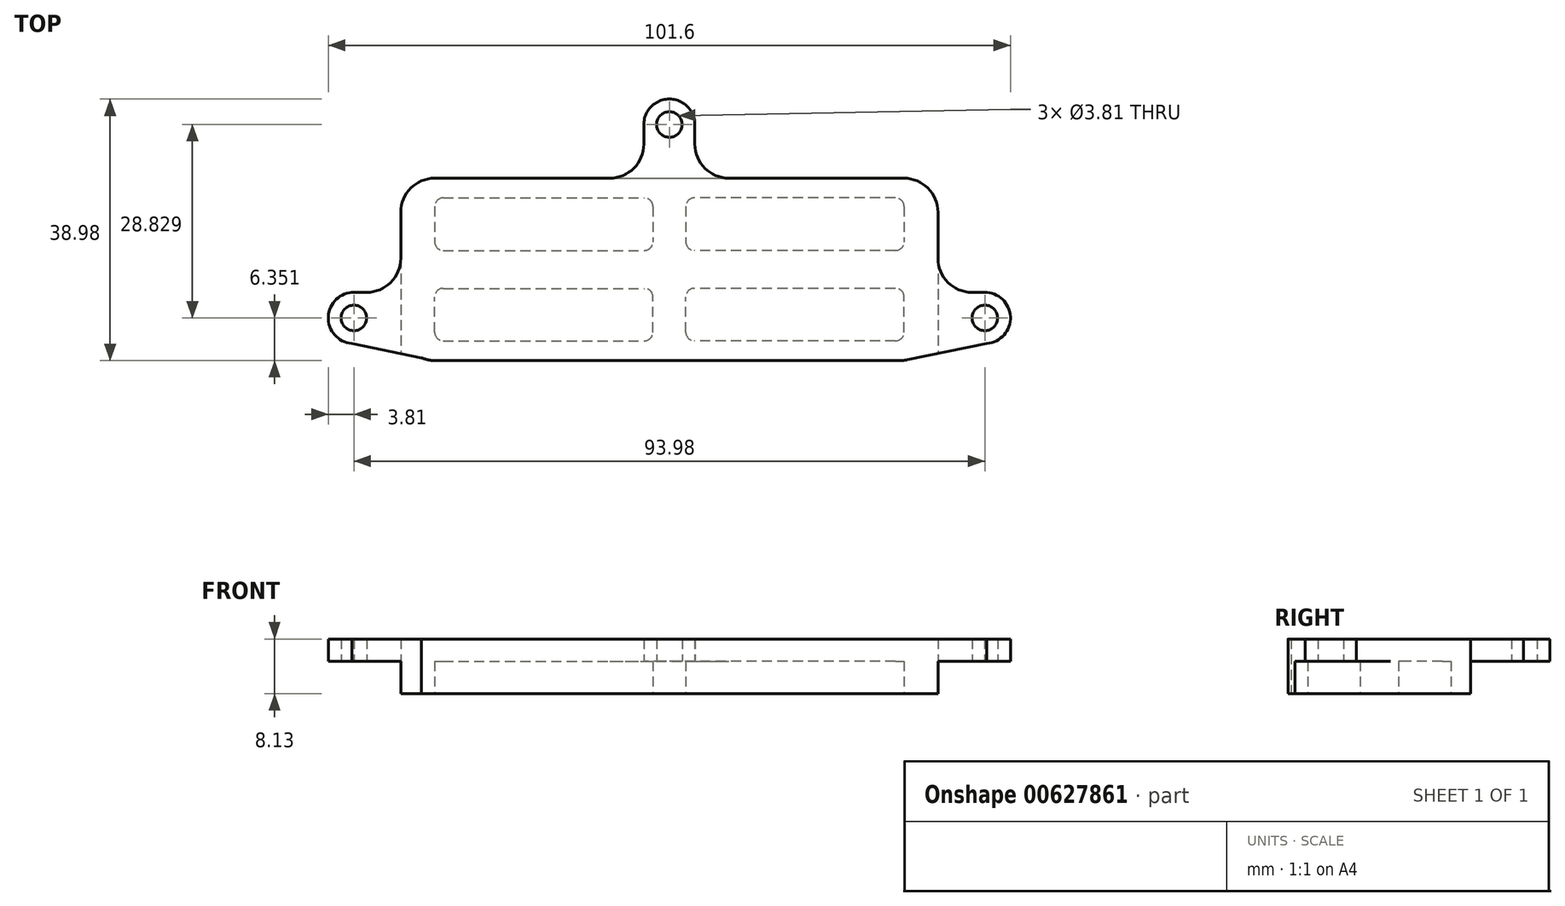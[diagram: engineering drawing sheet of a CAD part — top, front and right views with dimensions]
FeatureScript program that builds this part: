
annotation { "Feature Type Name" : "Feature", "Feature Type Description" : "" }
export const myFeature = defineFeature(function(context is Context, id is Id, definition is map)
    precondition{}
    {
        {
            var Q0;
            Q0=qCreatedBy(makeId("Top.planeOp"),FACE);
            var sketch = newSketch(context, id + "F0", { "sketchPlane" : qUnion([Q0])});
            skLineSegment(sketch, "E0.bottom", {"start": v(-34.93, 13.59) * mm, "end": v(-8.88, 13.59) * mm});
            skLineSegment(sketch, "E0.top", {"start": v(-34.93, -13.59) * mm, "end": v(34.4, -13.59) * mm});
            skLineSegment(sketch, "E0.left", {"start": v(-40, 8.5) * mm, "end": v(-40, 1.65) * mm});
            skLineSegment(sketch, "E0.right", {"start": v(40, 8.5) * mm, "end": v(40, 1.65) * mm});
            skPoint(sketch, "E0.middle", {"position": v(0, 0) * mm});
            skPoint(sketch, "E1", {"position": v(-47, -7.24) * mm});
            skPoint(sketch, "E2.MirrorP", {"position": v(47, -7.24) * mm});
            skPoint(sketch, "E3", {"position": v(0, 21.59) * mm});
            skPoint(sketch, "E4", {"position": v(-9.31, -13.59) * mm});
            skPoint(sketch, "E5.visualSharp", {"position": v(-40, 13.59) * mm});
            skArc(sketch, "E5.filletArc", {"start": v(-34.93, 13.59) * mm, "mid": v(-38.52, 12.1) * mm, "end": v(-40, 8.5) * mm});
            skArc(sketch, "E6.MirrorCS", {"start": v(-34.93, -13.59) * mm, "mid": v(-35.95, -13.48) * mm, "end": v(-36.94, -13.17) * mm});
            skArc(sketch, "E7.MirrorCS", {"start": v(34.93, 13.59) * mm, "mid": v(38.52, 12.1) * mm, "end": v(40, 8.5) * mm});
            skCircle(sketch, "E8", {"center": v(47, -7.24) * mm, "radius": 3.81 * mm});
            skCircle(sketch, "E9", {"center": v(-47, -7.24) * mm, "radius": 3.81 * mm});
            skCircle(sketch, "E10", {"center": v(0, 21.59) * mm, "radius": 3.8 * mm});
            skPoint(sketch, "E11.orphan", {"position": v(40, 13.59) * mm});
            skPoint(sketch, "E12.orphan", {"position": v(40, -13.59) * mm});
            skLineSegment(sketch, "E13", {"start": v(-3.8, 21.72) * mm, "end": v(-3.8, 18.67) * mm});
            skArc(sketch, "E14.filletArc", {"start": v(-8.88, 13.59) * mm, "mid": v(-5.29, 15.08) * mm, "end": v(-3.8, 18.67) * mm});
            skArc(sketch, "E15.MirrorCS", {"start": v(8.88, 13.59) * mm, "mid": v(5.29, 15.08) * mm, "end": v(3.8, 18.67) * mm});
            skLineSegment(sketch, "E16.MirrorCS", {"start": v(3.8, 21.72) * mm, "end": v(3.8, 18.67) * mm});
            skLineSegment(sketch, "E17", {"start": v(-47.04, -3.43) * mm, "end": v(-45.09, -3.43) * mm});
            skPoint(sketch, "E17.endSnap0", {"position": v(-40, -2.54) * mm});
            skPoint(sketch, "E18.newPointA", {"position": v(-40, -3.43) * mm});
            skPoint(sketch, "E18.newPointB", {"position": v(-40, -13.59) * mm});
            skArc(sketch, "E18.filletArc", {"start": v(-45.09, -3.43) * mm, "mid": v(-41.5, -1.94) * mm, "end": v(-40, 1.65) * mm});
            skArc(sketch, "E19.MirrorCS", {"start": v(45.09, -3.43) * mm, "mid": v(41.5, -1.94) * mm, "end": v(40, 1.65) * mm});
            skLineSegment(sketch, "E20.MirrorCS", {"start": v(47.04, -3.43) * mm, "end": v(45.09, -3.43) * mm});
            skLineSegment(sketch, "E21", {"start": v(47.3, -11.04) * mm, "end": v(35.43, -13.48) * mm});
            skPoint(sketch, "E22.orphan", {"position": v(40, -8.5) * mm});
            skPoint(sketch, "E23.visualSharp", {"position": v(34.93, -13.59) * mm});
            skArc(sketch, "E23.filletArc", {"start": v(34.4, -13.59) * mm, "mid": v(34.92, -13.56) * mm, "end": v(35.43, -13.48) * mm});
            skLineSegment(sketch, "E24.MirrorCS", {"start": v(-47.3, -11.04) * mm, "end": v(-35.43, -13.48) * mm});
            skPoint(sketch, "E25.orphan", {"position": v(-40, -8.5) * mm});
            skCircle(sketch, "E26", {"center": v(0, 21.59) * mm, "radius": 1.9 * mm});
            skCircle(sketch, "E27", {"center": v(-47, -7.24) * mm, "radius": 1.9 * mm});
            skCircle(sketch, "E28", {"center": v(47, -7.24) * mm, "radius": 1.9 * mm});
            skPoint(sketch, "E29.visualSharp", {"position": v(-34.16, 7.75) * mm});
            skPoint(sketch, "E30.orphan", {"position": v(-34.16, -7.75) * mm});
            skPoint(sketch, "E31.orphan", {"position": v(34.16, -7.75) * mm});
            skPoint(sketch, "E32.orphan", {"position": v(34.16, 7.75) * mm});
            skLineSegment(sketch, "E33", {"start": v(8.88, 13.59) * mm, "end": v(34.93, 13.59) * mm});
            skPoint(sketch, "E29.filletArc.end.orphan", {"position": v(-34.16, 5.2) * mm});
            skPoint(sketch, "E29.filletArc.start.orphan", {"position": v(-31.62, 7.75) * mm});
            skPoint(sketch, "E34.MirrorCS.end.orphan", {"position": v(-34.16, -5.2) * mm});
            skPoint(sketch, "E35.top.start.orphan", {"position": v(-31.62, -7.75) * mm});
            skPoint(sketch, "E36.MirrorCS.start.orphan", {"position": v(31.62, -7.75) * mm});
            skPoint(sketch, "E35.right.end.orphan", {"position": v(34.16, -5.2) * mm});
            skPoint(sketch, "E37.MirrorCS.end.orphan", {"position": v(34.16, 5.2) * mm});
            skPoint(sketch, "E37.MirrorCS.start.orphan", {"position": v(31.62, 7.75) * mm});
            skLineSegment(sketch, "E38", {"start": v(-40, 1.65) * mm, "end": v(-40, -12.54) * mm});
            skSolve(sketch);
        }
        {
            var Q0;
            Q0=qSketchRegion(id+"F0",true);
            extrude(context, id + "F1", {"entities" : qUnion([Q0]), "depth" : 3.3 * mm, "offsetDistance" : 25.4 * mm});
        }
        {
            var Q0;
            Q0=makeQuery(id+"F1.opExtrude","CAP_FACE",FACE,{"disambiguationData":[OSD([sQuery(id+"F0.wireOp",EDGE,"E0.bottom"),sQuery(id+"F0.wireOp",EDGE,"E0.top"),sQuery(id+"F0.wireOp",EDGE,"E0.left"),sQuery(id+"F0.wireOp",EDGE,"E0.right"),sQuery(id+"F0.wireOp",EDGE,"E5.filletArc"),sQuery(id+"F0.wireOp",EDGE,"E6.MirrorCS"),sQuery(id+"F0.wireOp",EDGE,"E7.MirrorCS"),sQuery(id+"F0.wireOp",EDGE,"E8"),sQuery(id+"F0.wireOp",EDGE,"E9"),sQuery(id+"F0.wireOp",EDGE,"E10"),sQuery(id+"F0.wireOp",EDGE,"E13"),sQuery(id+"F0.wireOp",EDGE,"E14.filletArc"),sQuery(id+"F0.wireOp",EDGE,"E15.MirrorCS"),sQuery(id+"F0.wireOp",EDGE,"E16.MirrorCS"),sQuery(id+"F0.wireOp",EDGE,"E17"),sQuery(id+"F0.wireOp",EDGE,"E18.filletArc"),sQuery(id+"F0.wireOp",EDGE,"E19.MirrorCS"),sQuery(id+"F0.wireOp",EDGE,"E20.MirrorCS"),sQuery(id+"F0.wireOp",EDGE,"E21"),sQuery(id+"F0.wireOp",EDGE,"E23.filletArc"),sQuery(id+"F0.wireOp",EDGE,"E24.MirrorCS"),sQuery(id+"F0.wireOp",EDGE,"E26"),sQuery(id+"F0.wireOp",EDGE,"E27"),sQuery(id+"F0.wireOp",EDGE,"E28"),sQuery(id+"F0.wireOp",EDGE,"E33")])],"isStart":true});
            var sketch = newSketch(context, id + "F2", { "sketchPlane" : qUnion([Q0])});
            skLineSegment(sketch, "E39", {"start": v(-40, -5.08) * mm, "end": v(-40, 12.54) * mm});
            skLineSegment(sketch, "E40.MirrorCS", {"start": v(40, -5.08) * mm, "end": v(40, 12.54) * mm});
            skLineSegment(sketch, "E41", {"start": v(-13.13, -13.59) * mm, "end": v(9.64, -13.59) * mm});
            skSolve(sketch);
        }
        {
            var Q0;
            Q0=qSketchRegion(id+"F2",true);
            var Q1;
            Q1=makeQuery(id+"F2.imprint","IMPRINT",FACE,{"disambiguationData":[TD([[makeQuery(id+"F2.imprint","IMPRINT",EDGE,{"derivedFrom":makeQuery(id+"F1.opExtrude","CAP_EDGE",EDGE,{"disambiguationData":[OSD([sQuery(id+"F0.wireOp",EDGE,"E0.top")])],"isStart":true})}),-1.0]])]});
            extrude(context, id + "F3", {"entities" : qUnion([Q0, Q1]), "operationType" : NewBodyOperationType.ADD, "depth" : 4.83 * mm, "offsetDistance" : 25.4 * mm});
        }
        {
            var Q0;
            Q0=makeQuery(id+"F3.opExtrude","CAP_FACE",FACE,{"disambiguationData":[OSD([sQuery(id+"F0.wireOp",EDGE,"E0.bottom"),sQuery(id+"F0.wireOp",EDGE,"E0.top"),sQuery(id+"F0.wireOp",EDGE,"E0.right"),sQuery(id+"F0.wireOp",EDGE,"E5.filletArc"),sQuery(id+"F0.wireOp",EDGE,"E6.MirrorCS"),sQuery(id+"F0.wireOp",EDGE,"E7.MirrorCS"),sQuery(id+"F0.wireOp",EDGE,"E21"),sQuery(id+"F0.wireOp",EDGE,"E23.filletArc"),sQuery(id+"F0.wireOp",EDGE,"E24.MirrorCS"),sQuery(id+"F2.wireOp",EDGE,"E39"),sQuery(id+"F2.wireOp",EDGE,"E40.MirrorCS"),sQuery(id+"F2.wireOp",EDGE,"E41")])],"isStart":false});
            var sketch = newSketch(context, id + "F4", { "sketchPlane" : qUnion([Q0])});
            skLineSegment(sketch, "E42.MirrorCS", {"start": v(-33.69, -2.83) * mm, "end": v(-3.72, -2.83) * mm});
            skLineSegment(sketch, "E43.MirrorCS", {"start": v(-2.45, -9.38) * mm, "end": v(-2.45, -4.1) * mm});
            skLineSegment(sketch, "E44.MirrorCS", {"start": v(-33.69, -10.65) * mm, "end": v(-3.72, -10.65) * mm});
            skLineSegment(sketch, "E45.MirrorCS", {"start": v(-34.96, -9.38) * mm, "end": v(-34.96, -4.1) * mm});
            skPoint(sketch, "E46.visualSharp", {"position": v(-34.96, -2.83) * mm});
            skArc(sketch, "E46.filletArc", {"start": v(-33.69, -2.83) * mm, "mid": v(-34.58, -3.2) * mm, "end": v(-34.96, -4.1) * mm});
            skPoint(sketch, "E47.visualSharp", {"position": v(-2.45, -2.83) * mm});
            skArc(sketch, "E47.filletArc", {"start": v(-2.45, -4.1) * mm, "mid": v(-2.82, -3.2) * mm, "end": v(-3.72, -2.83) * mm});
            skPoint(sketch, "E48.visualSharp", {"position": v(-2.45, -10.65) * mm});
            skArc(sketch, "E48.filletArc", {"start": v(-3.72, -10.65) * mm, "mid": v(-2.82, -10.27) * mm, "end": v(-2.45, -9.38) * mm});
            skPoint(sketch, "E49.visualSharp", {"position": v(-34.96, -10.65) * mm});
            skArc(sketch, "E49.filletArc", {"start": v(-34.96, -9.38) * mm, "mid": v(-34.58, -10.27) * mm, "end": v(-33.69, -10.65) * mm});
            skLineSegment(sketch, "E50.MirrorCS", {"start": v(2.45, -9.38) * mm, "end": v(2.45, -4.1) * mm});
            skArc(sketch, "E51.MirrorCS", {"start": v(2.45, -4.1) * mm, "mid": v(2.82, -3.2) * mm, "end": v(3.72, -2.83) * mm});
            skArc(sketch, "E52.MirrorCS", {"start": v(3.72, -10.65) * mm, "mid": v(2.82, -10.27) * mm, "end": v(2.45, -9.38) * mm});
            skLineSegment(sketch, "E53.MirrorCS", {"start": v(33.69, -10.65) * mm, "end": v(3.72, -10.65) * mm});
            skArc(sketch, "E54.MirrorCS", {"start": v(34.96, -9.38) * mm, "mid": v(34.58, -10.27) * mm, "end": v(33.69, -10.65) * mm});
            skLineSegment(sketch, "E55.MirrorCS", {"start": v(34.96, -9.38) * mm, "end": v(34.96, -4.1) * mm});
            skArc(sketch, "E56.MirrorCS", {"start": v(33.69, -2.83) * mm, "mid": v(34.58, -3.2) * mm, "end": v(34.96, -4.1) * mm});
            skLineSegment(sketch, "E57.MirrorCS", {"start": v(33.69, -2.83) * mm, "end": v(3.72, -2.83) * mm});
            skLineSegment(sketch, "E58.MirrorCS", {"start": v(-33.69, 2.83) * mm, "end": v(-3.72, 2.83) * mm});
            skArc(sketch, "E59.MirrorCS", {"start": v(-2.45, 4.1) * mm, "mid": v(-2.82, 3.2) * mm, "end": v(-3.72, 2.83) * mm});
            skLineSegment(sketch, "E60.MirrorCS", {"start": v(-2.45, 9.38) * mm, "end": v(-2.45, 4.1) * mm});
            skArc(sketch, "E61.MirrorCS", {"start": v(-3.72, 10.65) * mm, "mid": v(-2.82, 10.27) * mm, "end": v(-2.45, 9.38) * mm});
            skLineSegment(sketch, "E62.MirrorCS", {"start": v(-33.69, 10.65) * mm, "end": v(-3.72, 10.65) * mm});
            skArc(sketch, "E63.MirrorCS", {"start": v(-34.96, 9.38) * mm, "mid": v(-34.58, 10.27) * mm, "end": v(-33.69, 10.65) * mm});
            skLineSegment(sketch, "E64.MirrorCS", {"start": v(-34.96, 9.38) * mm, "end": v(-34.96, 4.1) * mm});
            skArc(sketch, "E65.MirrorCS", {"start": v(-33.69, 2.83) * mm, "mid": v(-34.58, 3.2) * mm, "end": v(-34.96, 4.1) * mm});
            skLineSegment(sketch, "E66.MirrorCS", {"start": v(2.45, 9.38) * mm, "end": v(2.45, 4.1) * mm});
            skArc(sketch, "E67.MirrorCS", {"start": v(3.72, 10.65) * mm, "mid": v(2.82, 10.27) * mm, "end": v(2.45, 9.38) * mm});
            skLineSegment(sketch, "E68.MirrorCS", {"start": v(33.69, 10.65) * mm, "end": v(3.72, 10.65) * mm});
            skArc(sketch, "E69.MirrorCS", {"start": v(34.96, 9.38) * mm, "mid": v(34.58, 10.27) * mm, "end": v(33.69, 10.65) * mm});
            skLineSegment(sketch, "E70.MirrorCS", {"start": v(34.96, 9.38) * mm, "end": v(34.96, 4.1) * mm});
            skArc(sketch, "E71.MirrorCS", {"start": v(33.69, 2.83) * mm, "mid": v(34.58, 3.2) * mm, "end": v(34.96, 4.1) * mm});
            skLineSegment(sketch, "E72.MirrorCS", {"start": v(33.69, 2.83) * mm, "end": v(3.72, 2.83) * mm});
            skArc(sketch, "E73.MirrorCS", {"start": v(2.45, 4.1) * mm, "mid": v(2.82, 3.2) * mm, "end": v(3.72, 2.83) * mm});
            skSolve(sketch);
        }
        {
            var Q0;
            Q0=makeQuery(id+"F4.imprint","IMPRINT",FACE,{"disambiguationData":[TD([[makeQuery(id+"F4.imprint","IMPRINT",EDGE,{"derivedFrom":sQuery(id+"F4.wireOp",EDGE,"E58.MirrorCS")}),1.0]])]});
            var Q1;
            Q1=makeQuery(id+"F4.imprint","IMPRINT",FACE,{"disambiguationData":[TD([[makeQuery(id+"F4.imprint","IMPRINT",EDGE,{"derivedFrom":sQuery(id+"F4.wireOp",EDGE,"E66.MirrorCS")}),1.0]])]});
            var Q2;
            Q2=makeQuery(id+"F4.imprint","IMPRINT",FACE,{"disambiguationData":[TD([[makeQuery(id+"F4.imprint","IMPRINT",EDGE,{"derivedFrom":sQuery(id+"F4.wireOp",EDGE,"E42.MirrorCS")}),-1.0]])]});
            var Q3;
            Q3=makeQuery(id+"F4.imprint","IMPRINT",FACE,{"disambiguationData":[TD([[makeQuery(id+"F4.imprint","IMPRINT",EDGE,{"derivedFrom":sQuery(id+"F4.wireOp",EDGE,"E50.MirrorCS")}),-1.0]])]});
            extrude(context, id + "F5", {"entities" : qUnion([Q0, Q1, Q2, Q3]), "operationType" : NewBodyOperationType.REMOVE, "oppositeDirection" : true, "depth" : 4.83 * mm, "offsetDistance" : 25.4 * mm});
        }
    });
